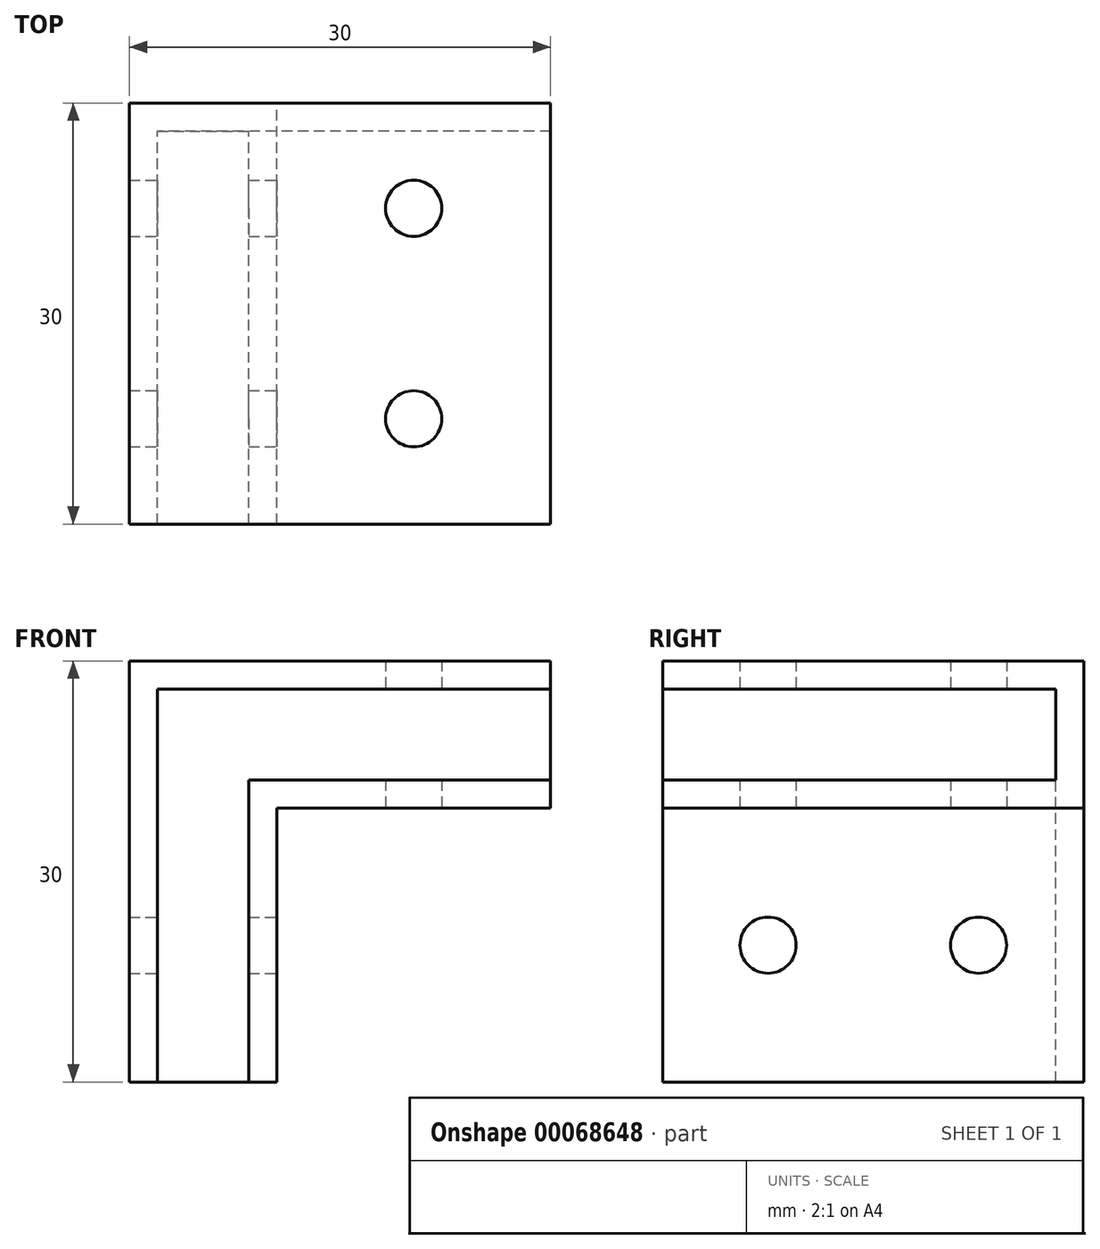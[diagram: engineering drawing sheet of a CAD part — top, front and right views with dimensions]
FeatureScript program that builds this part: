
annotation { "Feature Type Name" : "Feature", "Feature Type Description" : "" }
export const myFeature = defineFeature(function(context is Context, id is Id, definition is map)
    precondition{}
    {
        {
            assignVariable(context, id + "F0", {"name" : "WallThickness", "anyValue" : 2});
        }
        {
            assignVariable(context, id + "F1", {"name" : "BracketHeight", "anyValue" : 30});
        }
        {
            var Q0;
            Q0=qCreatedBy(makeId("Front.planeOp"),FACE);
            var sketch = newSketch(context, id + "F2", { "sketchPlane" : qUnion([Q0])});
            skLineSegment(sketch, "E0.bottom", {"start": v(0, 0) * mm, "end": v(28, 0) * mm});
            skLineSegment(sketch, "E0.top", {"start": v(0, -6.5) * mm, "end": v(28, -6.5) * mm});
            skLineSegment(sketch, "E0.left", {"start": v(0, 0) * mm, "end": v(0, -6.5) * mm});
            skLineSegment(sketch, "E0.right", {"start": v(28, 0) * mm, "end": v(28, -6.5) * mm});
            skLineSegment(sketch, "E1", {"start": v(0, -6.5) * mm, "end": v(0, -28) * mm});
            skLineSegment(sketch, "E2", {"start": v(0, -28) * mm, "end": v(51.52, -28) * mm, "construction": true});
            skLineSegment(sketch, "E3", {"start": v(0, -28) * mm, "end": v(6.5, -28) * mm});
            skLineSegment(sketch, "E4", {"start": v(6.5, -28) * mm, "end": v(6.5, -6.5) * mm});
            skLineSegment(sketch, "E5", {"start": v(28, 0) * mm, "end": v(28, 2) * mm});
            skLineSegment(sketch, "E6", {"start": v(0, -28) * mm, "end": v(-2, -28) * mm});
            skLineSegment(sketch, "E7", {"start": v(0, 0) * mm, "end": v(0, 2) * mm});
            skLineSegment(sketch, "E8", {"start": v(0, 0) * mm, "end": v(-2, 0) * mm});
            skLineSegment(sketch, "E9", {"start": v(28, 2) * mm, "end": v(0, 2) * mm});
            skLineSegment(sketch, "E10", {"start": v(0, 2) * mm, "end": v(-25.18, 2) * mm, "construction": true});
            skLineSegment(sketch, "E11", {"start": v(-2, -28) * mm, "end": v(-2, 0) * mm});
            skLineSegment(sketch, "E12", {"start": v(-2, 0) * mm, "end": v(-2, 2) * mm});
            skLineSegment(sketch, "E13", {"start": v(-2, 2) * mm, "end": v(0, 2) * mm});
            skLineSegment(sketch, "E14", {"start": v(28, -6.5) * mm, "end": v(28, -8.5) * mm});
            skLineSegment(sketch, "E15", {"start": v(6.5, -28) * mm, "end": v(8.5, -28) * mm});
            skLineSegment(sketch, "E16", {"start": v(6.5, -6.5) * mm, "end": v(6.5, -8.5) * mm, "construction": true});
            skLineSegment(sketch, "E17", {"start": v(6.5, -6.5) * mm, "end": v(8.5, -6.5) * mm, "construction": true});
            skLineSegment(sketch, "E18", {"start": v(8.5, -6.5) * mm, "end": v(8.5, -28) * mm});
            skLineSegment(sketch, "E19", {"start": v(6.5, -8.5) * mm, "end": v(8.5, -8.5) * mm});
            skLineSegment(sketch, "E20", {"start": v(28, -8.5) * mm, "end": v(8.5, -8.5) * mm});
            skLineSegment(sketch, "E21", {"start": v(28, 2) * mm, "end": v(-2, 2) * mm, "construction": true});
            skSolve(sketch);
        }
        {
            var Q0;
            Q0 = qSketchRegion(id + "F2", true);
            extrude(context, id + "F3", {"entities" : qUnion([Q0]), "depth" : (getVariable(context, 'WallThickness')) * mm});
        }
        {
            var Q0;
            Q0=makeQuery(id+"F2.imprint","IMPRINT",FACE,{"disambiguationData":[TD([[makeQuery(id+"F2.imprint","IMPRINT",EDGE,{"derivedFrom":sQuery(id+"F2.wireOp",EDGE,"E0.bottom")}),1.0]])]});
            var Q1;
            Q1=makeQuery(id+"F2.imprint","IMPRINT",FACE,{"disambiguationData":[TD([[makeQuery(id+"F2.imprint","IMPRINT",EDGE,{"derivedFrom":sQuery(id+"F2.wireOp",EDGE,"E7")}),1.0]])]});
            var Q2;
            Q2=makeQuery(id+"F2.imprint","IMPRINT",FACE,{"disambiguationData":[TD([[makeQuery(id+"F2.imprint","IMPRINT",EDGE,{"derivedFrom":sQuery(id+"F2.wireOp",EDGE,"E0.left")}),-1.0]])]});
            var Q3;
            {var subQ0=sQuery(id+"F2.wireOp",EDGE,"E14");Q3=makeQuery(id+"F2.imprint","IMPRINT",FACE,{"disambiguationData":[TD([[makeQuery(id+"F2.imprint","IMPRINT",EDGE,{"derivedFrom":subQ0}),-1.0]])]});}
            var Q4;
            {var subQ5=sQuery(id+"F2.wireOp",EDGE,"E19");Q4=makeQuery(id+"F2.imprint","IMPRINT",FACE,{"disambiguationData":[TD([[makeQuery(id+"F2.imprint","IMPRINT",EDGE,{"derivedFrom":subQ5}),1.0]])]});}
            var Q5;
            {var subQ0=sQuery(id+"F2.wireOp",EDGE,"E15");Q5=makeQuery(id+"F2.imprint","IMPRINT",FACE,{"disambiguationData":[TD([[makeQuery(id+"F2.imprint","IMPRINT",EDGE,{"derivedFrom":subQ0}),1.0]])]});}
            extrude(context, id + "F4", {"entities" : qUnion([Q0, Q1, Q2, Q3, Q4, Q5]), "operationType" : NewBodyOperationType.ADD, "depth" : (getVariable(context, 'BracketHeight')) * mm});
        }
        {
            var Q0;
            {var subQ0=sQuery(id+"F2.wireOp",EDGE,"E20");Q0=makeQuery(id+"F4.boolean.opBoolean","MERGE",FACE,{"derivedFrom":[makeQuery(id+"F3.opExtrude","SWEPT_FACE",FACE,{"disambiguationData":[OSD([subQ0])]}),makeQuery(id+"F4.opExtrude","SWEPT_FACE",FACE,{"disambiguationData":[OSD([subQ0])]})]});}
            var sketch = newSketch(context, id + "F5", { "sketchPlane" : qUnion([Q0])});
            skLineSegment(sketch, "E22", {"start": v(18.25, 30) * mm, "end": v(18.25, 0) * mm, "construction": true});
            skLineSegment(sketch, "E23", {"start": v(18.25, 0) * mm, "end": v(18.25, 15) * mm, "construction": true});
            skLineSegment(sketch, "E24", {"start": v(18.25, 15) * mm, "end": v(18.25, 7.5) * mm, "construction": true});
            skLineSegment(sketch, "E25", {"start": v(18.25, 15) * mm, "end": v(18.25, 30) * mm, "construction": true});
            skLineSegment(sketch, "E26", {"start": v(18.25, 15) * mm, "end": v(18.25, 22.5) * mm, "construction": true});
            skCircle(sketch, "E27", {"center": v(18.25, 22.5) * mm, "radius": 2 * mm});
            skCircle(sketch, "E28", {"center": v(18.25, 7.5) * mm, "radius": 2 * mm});
            skSolve(sketch);
        }
        {
            var Q0;
            Q0 = qSketchRegion(id + "F5", true);
            extrude(context, id + "F6", {"entities" : qUnion([Q0]), "operationType" : NewBodyOperationType.REMOVE, "oppositeDirection" : true, "depth" : 25 * mm});
        }
        {
            var Q0;
            {var subQ0=sQuery(id+"F2.wireOp",EDGE,"E18");Q0=makeQuery(id+"F4.boolean.opBoolean","MERGE",FACE,{"derivedFrom":[makeQuery(id+"F3.opExtrude","SWEPT_FACE",FACE,{"disambiguationData":[OSD([subQ0])]}),makeQuery(id+"F4.opExtrude","SWEPT_FACE",FACE,{"disambiguationData":[OSD([subQ0])]})]});}
            var sketch = newSketch(context, id + "F7", { "sketchPlane" : qUnion([Q0])});
            skLineSegment(sketch, "E29", {"start": v(-30, -18.25) * mm, "end": v(0, -18.25) * mm, "construction": true});
            skLineSegment(sketch, "E30", {"start": v(-30, -18.25) * mm, "end": v(-15, -18.25) * mm, "construction": true});
            skLineSegment(sketch, "E31", {"start": v(-15, -18.25) * mm, "end": v(-22.5, -18.25) * mm, "construction": true});
            skLineSegment(sketch, "E32", {"start": v(-15, -18.25) * mm, "end": v(0, -18.25) * mm, "construction": true});
            skLineSegment(sketch, "E33", {"start": v(-15, -18.25) * mm, "end": v(-7.5, -18.25) * mm, "construction": true});
            skCircle(sketch, "E34", {"center": v(-22.5, -18.25) * mm, "radius": 2 * mm});
            skCircle(sketch, "E35", {"center": v(-7.5, -18.25) * mm, "radius": 2 * mm});
            skSolve(sketch);
        }
        {
            var Q0;
            Q0 = qSketchRegion(id + "F7", true);
            extrude(context, id + "F8", {"entities" : qUnion([Q0]), "operationType" : NewBodyOperationType.REMOVE, "oppositeDirection" : true, "depth" : 25 * mm});
        }
    });
